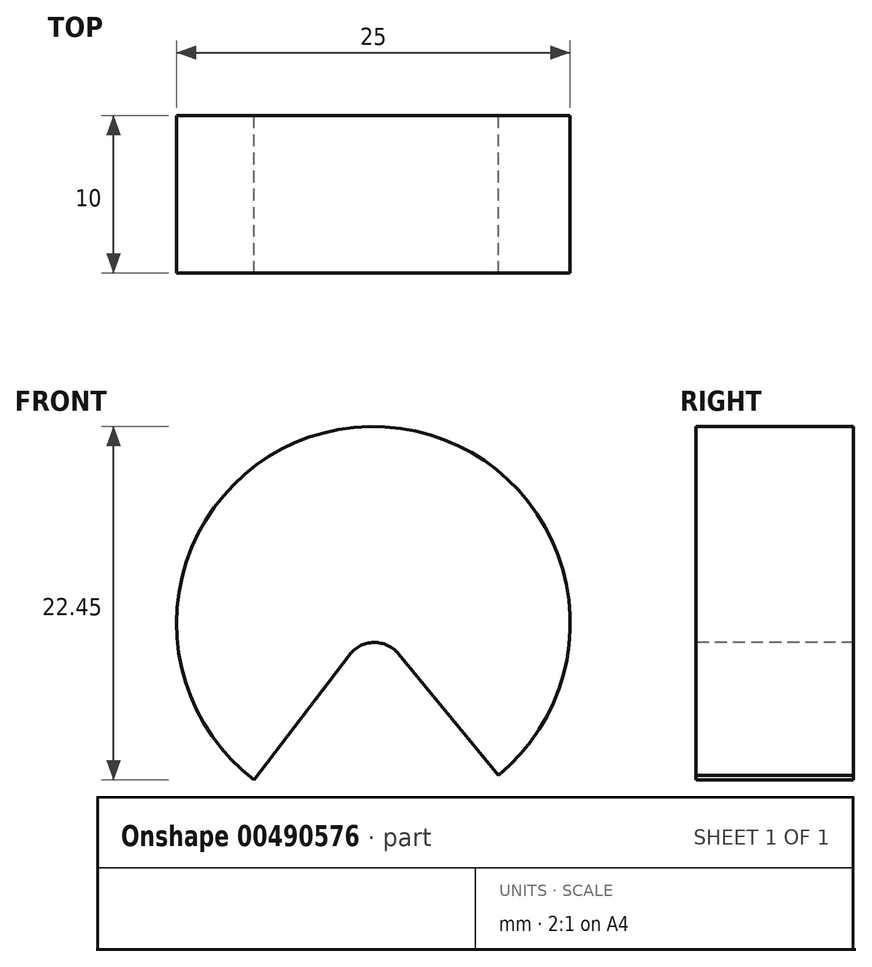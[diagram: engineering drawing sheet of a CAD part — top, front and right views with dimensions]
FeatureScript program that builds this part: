
annotation { "Feature Type Name" : "Feature", "Feature Type Description" : "" }
export const myFeature = defineFeature(function(context is Context, id is Id, definition is map)
    precondition{}
    {
        {
            var Q0;
            Q0=qCreatedBy(makeId("Front.planeOp"),FACE);
            var sketch = newSketch(context, id + "F0", { "sketchPlane" : qUnion([Q0])});
            skCircle(sketch, "E0", {"center": v(0, 0) * mm, "radius": 12.5 * mm});
            skSolve(sketch);
        }
        {
            var Q0;
            Q0 = qSketchRegion(id + "F0", true);
            extrude(context, id + "F1", {"entities" : qUnion([Q0]), "depth" : 10 * mm});
        }
        {
            var Q0;
            Q0=makeQuery(id+"F1.opExtrude","CAP_FACE",FACE,{"disambiguationData":[OSD([sQuery(id+"F0.wireOp",EDGE,"E0")])],"isStart":true});
            var sketch = newSketch(context, id + "F2", { "sketchPlane" : qUnion([Q0])});
            skLineSegment(sketch, "E1", {"start": v(-7.95, -9.65) * mm, "end": v(0, 0) * mm});
            skLineSegment(sketch, "E2", {"start": v(0, 0) * mm, "end": v(7.57, -9.95) * mm});
            skArc(sketch, "E3.0", {"start": v(-7.95, -9.65) * mm, "mid": v(-0.24, -12.5) * mm, "end": v(7.57, -9.95) * mm});
            skSolve(sketch);
        }
        {
            var Q0;
            Q0 = qSketchRegion(id + "F2", true);
            extrude(context, id + "F3", {"entities" : qUnion([Q0]), "operationType" : NewBodyOperationType.REMOVE, "oppositeDirection" : true, "depth" : 25.4 * mm});
        }
        {
            var Q0;
            Q0=makeQuery(id+"F3.boolean.opBoolean","COPY",EDGE,{"derivedFrom":makeQuery(id+"F3.opExtrude","SWEPT_EDGE",EDGE,{"disambiguationData":[OSD([sQuery(id+"F2.wireOp",EDGE,"E1"),sQuery(id+"F2.wireOp",EDGE,"E2")])]})});
            fillet(context, id + "F4", {"entities" : qUnion([Q0]), "radius" : 2 * mm, "tangentPropagation" : true, "allowEdgeOverflow" : false});
        }
    });
